# Revit family: Hager-Univers-IP44-D205-H950-Cl.II-Encl-ES-es
name_source: partatom
category: Equipement électrique
units: mm (PartAtom-declared; Revit-internal decimal feet)

## family parameters
Configuration du panneau = Deux colonnes, circuits au sein
Cote de connecteur circulaire = Utiliser le diamètre
Couper avec des vides une fois chargée = Non
Hôte = Face
Partagée = Non
Point de calcul de pièce = Non
Type d'élément = Tableau de raccordement

## types (5) — shared parameters
Commentaires du type = Univers
EF000003 - Tipo de montaje = EV000384 - Montado superficial (escayola)
EF000007 - Color = EV000202 - Blanco
EF000040 - Altura = 950 mm  [stored 3.1168 ft]
EF000049 - Profundidad = 205 mm  [stored 0.672572 ft]
EF000116 - Número RAL = 9010
EF000118 - Con placa de montaje = Non
EF000218 - Profundidad de instalación = 205 mm  [stored 0.672572 ft]
EF000266 - Número de filas = 6
EF001088 - Posibilidad de extensión = Oui
EF001596 - Material de la carcasa = EV000179 - Acero
EF001613 - Integridad del circuito = EV000494 - Ninguno
EF003532 - Adecuado para uso en exteriores = Non
EF004293 - Resistencia al impacto (IK) = EV006815 - IK09
EF005474 - Grado de protección (IP) = EV006418 - IP44
EF006244 - Tapa/puerta transparente = Non
EF006306 - Con cierre = Non
EF007800 - Adecuado para la protección contra rayos = Non
EF008873 - Corriente nominal (In) = 250 A
EF009170 - Espesor del material de la caja = 1 mm  [stored 0.00328084 ft]
EF009171 - Espesor puerta/tapa = 1 mm  [stored 0.00328084 ft]
EF009212 - Versión de la cubierta = EV000116 - Cerrado
EF015940 - Tapa con alivio de sobrepresión = Non
Fabricant = Hager
HG000002 - Con puerta o tapa = Oui
HG000003 - Gama = Univers
HG000006 - Empotrado = Non
HG000023 - Caja de doble sección = Non
HG000024 - Altura de la sección inferior = 800 mm  [stored 2.62467 ft]
HG000026 - Instalación en suelo = Non
zero-valued in all types: Elévation par défaut, HG000027 - Altura de zócalo

## per-type parameters (varying)
| type | EF000008 - Anchura | EF000339 - Tipo de cubierta | EF000437 - Número de entradas de conductos de cables | EF001131 - Profundidad interna | EF002950 - Anchura de unidades de división | EF004427 - Número de módulos | EF004464 - Tipo de puerta | EF009554 - Número de aberturas para placas-brida | HG000004 - Referencia del fabricante | HG000009 - Puerta batiente doble | HG000010 - Puertas asimétricas |
| Montado superficial (escayola) IP44 A1050 A950 P205  - FP64SN2 | 1050 mm | EV004216 - Puerta | 8 | 130 mm  [stored 0.426509 ft] | 48 | 288 | EV003602 - Doble | 8 | FP64SN2 | Oui | Non |
| Montado superficial (escayola) IP44 A1300 A950 P205  - FP65SN2 | 1300 mm  [stored 4.26509 ft] | EV004216 - Puerta | 10 | 130 mm  [stored 0.426509 ft] | 60 | 360 | EV003602 - Doble | 10 | FP65SN2 | Oui | Oui |
| Montado superficial (escayola) IP44 A300 A950 P205  - FP61SN2 | 300 mm | EV001012 - Cubrir | 2 | 143 mm | 12 | 72 | EV002646 - Único | 2 | FP61SN2 | Non | Non |
| Montado superficial (escayola) IP44 A550 A950 P205  - FP62SN2 | 550 mm | EV001012 - Cubrir | 4 | 143 mm | 24 | 144 | EV002646 - Único | 4 | FP62SN2 | Non | Non |
| Montado superficial (escayola) IP44 A800 A950 P205  - FP63SN2 | 800 mm  [stored 2.62467 ft] | EV004216 - Puerta | 6 | 130 mm  [stored 0.426509 ft] | 36 | 216 | EV002646 - Único | 6 | FP63SN2 | Non | Non |

note: [stored X ft] marks values corroborated as IEEE doubles in the binary element streams (Revit-internal decimal feet)

## geometry (parser evidence)
native form markers: Sweep x10
no freeform markers — native parametric forms only
